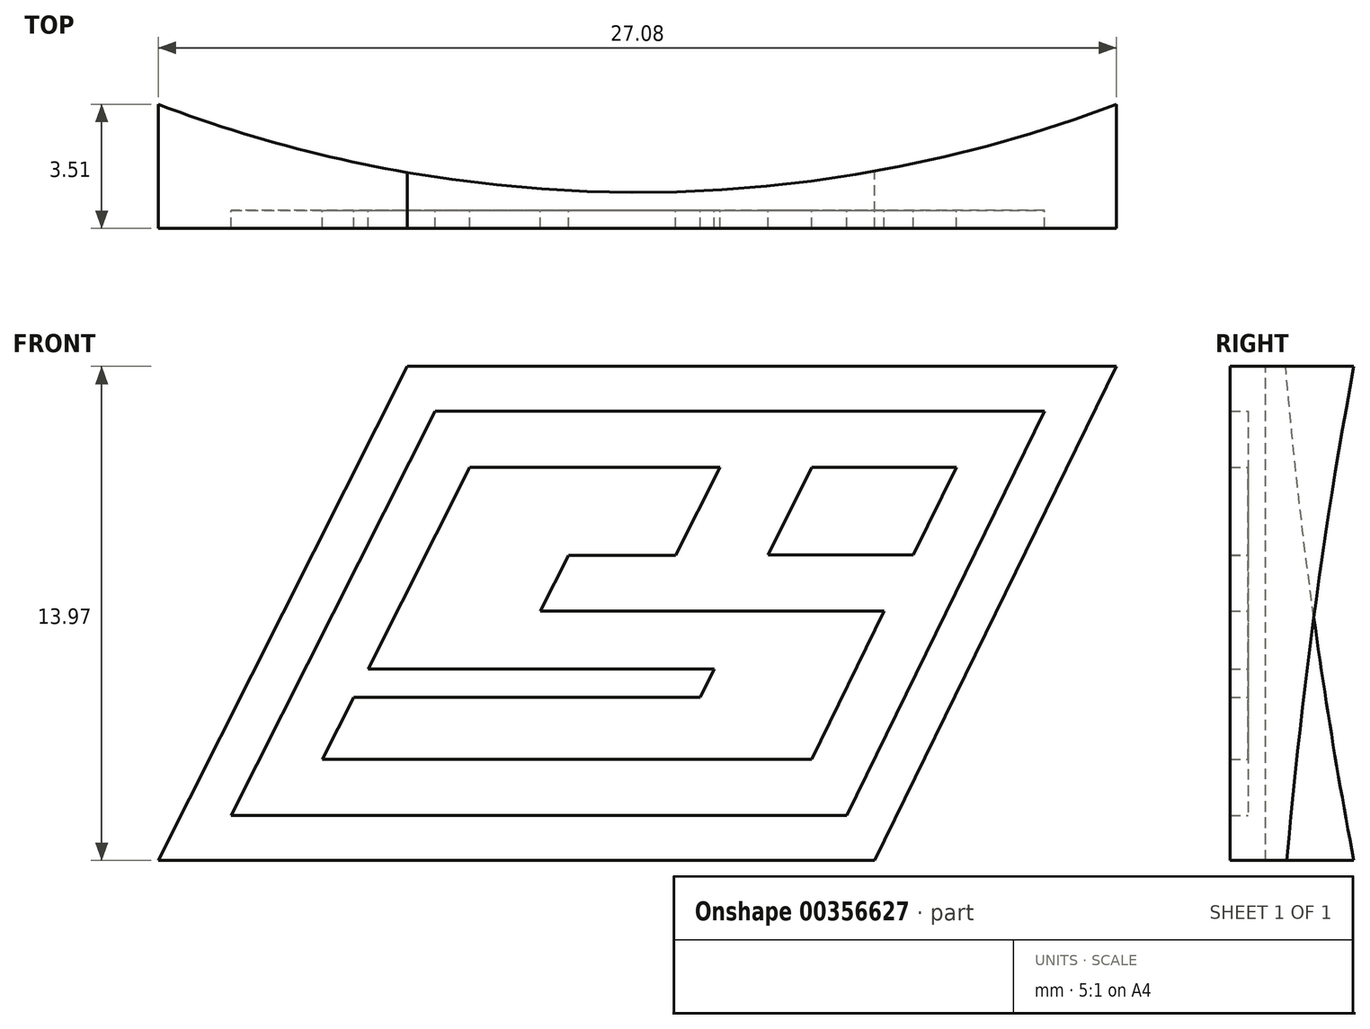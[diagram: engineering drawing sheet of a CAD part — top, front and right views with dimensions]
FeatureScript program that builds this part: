
annotation { "Feature Type Name" : "Feature", "Feature Type Description" : "" }
export const myFeature = defineFeature(function(context is Context, id is Id, definition is map)
    precondition{}
    {
        {
            var Q0;
            Q0=qCreatedBy(makeId("Front.planeOp"),FACE);
            var sketch = newSketch(context, id + "F0", { "sketchPlane" : qUnion([Q0])});
            skLineSegment(sketch, "E0", {"start": v(-12.43, 33) * mm, "end": v(15.1, 33) * mm, "construction": true});
            skLineSegment(sketch, "E1", {"start": v(15.1, 33) * mm, "end": v(6.9, 16.48) * mm, "construction": true});
            skLineSegment(sketch, "E2", {"start": v(6.9, 16.48) * mm, "end": v(-20.75, 16.48) * mm, "construction": true});
            skLineSegment(sketch, "E3", {"start": v(-20.75, 16.48) * mm, "end": v(-12.43, 33) * mm, "construction": true});
            skLineSegment(sketch, "E4", {"start": v(-12.43, 33) * mm, "end": v(1.74, 33) * mm});
            skLineSegment(sketch, "E5", {"start": v(1.74, 33) * mm, "end": v(-0.77, 28.01) * mm});
            skLineSegment(sketch, "E6", {"start": v(-0.77, 28.01) * mm, "end": v(-6.84, 28.01) * mm});
            skLineSegment(sketch, "E7", {"start": v(-6.84, 28.01) * mm, "end": v(-8.43, 24.86) * mm});
            skLineSegment(sketch, "E8", {"start": v(-8.43, 24.86) * mm, "end": v(11, 24.86) * mm});
            skPoint(sketch, "E8.endSnap0", {"position": v(11, 24.74) * mm});
            skLineSegment(sketch, "E9", {"start": v(11, 24.86) * mm, "end": v(6.9, 16.48) * mm});
            skLineSegment(sketch, "E10", {"start": v(-20.75, 16.48) * mm, "end": v(-18.97, 20) * mm});
            skLineSegment(sketch, "E11", {"start": v(-18.97, 20) * mm, "end": v(0.6, 20) * mm});
            skLineSegment(sketch, "E12", {"start": v(0.6, 20) * mm, "end": v(1.4, 21.6) * mm});
            skLineSegment(sketch, "E13", {"start": v(1.4, 21.6) * mm, "end": v(-18.16, 21.6) * mm});
            skLineSegment(sketch, "E14", {"start": v(-18.16, 21.6) * mm, "end": v(-12.43, 33) * mm});
            skLineSegment(sketch, "E15", {"start": v(6.9, 33) * mm, "end": v(4.45, 28.06) * mm});
            skLineSegment(sketch, "E16", {"start": v(4.45, 28.06) * mm, "end": v(12.65, 28.06) * mm});
            skLineSegment(sketch, "E17", {"start": v(12.65, 28.06) * mm, "end": v(15.1, 33) * mm});
            skLineSegment(sketch, "E18", {"start": v(-20.75, 16.48) * mm, "end": v(6.9, 16.48) * mm});
            skLineSegment(sketch, "E19", {"start": v(6.9, 33) * mm, "end": v(15.1, 33) * mm});
            skSolve(sketch);
        }
        {
            var Q0;
            Q0=qCreatedBy(makeId("Front.planeOp"),FACE);
            var sketch = newSketch(context, id + "F1", { "sketchPlane" : qUnion([Q0])});
            skLineSegment(sketch, "E20", {"start": v(-25.9, 13.3) * mm, "end": v(8.88, 13.3) * mm});
            skLineSegment(sketch, "E21", {"start": v(8.88, 13.3) * mm, "end": v(20.07, 36.17) * mm});
            skLineSegment(sketch, "E22", {"start": v(20.07, 36.17) * mm, "end": v(-14.38, 36.17) * mm});
            skLineSegment(sketch, "E23", {"start": v(-14.38, 36.17) * mm, "end": v(-25.9, 13.3) * mm});
            skSolve(sketch);
        }
        {
            var Q0;
            Q0=qCreatedBy(makeId("Front.planeOp"),FACE);
            var sketch = newSketch(context, id + "F2", { "sketchPlane" : qUnion([Q0])});
            skLineSegment(sketch, "E24", {"start": v(-30.02, 10.77) * mm, "end": v(-15.95, 38.71) * mm});
            skLineSegment(sketch, "E25", {"start": v(-15.95, 38.71) * mm, "end": v(24.14, 38.71) * mm});
            skLineSegment(sketch, "E26", {"start": v(24.14, 38.71) * mm, "end": v(10.47, 10.77) * mm});
            skLineSegment(sketch, "E27", {"start": v(10.47, 10.77) * mm, "end": v(-30.02, 10.77) * mm});
            skLineSegment(sketch, "E28.0", {"start": v(8.88, 13.3) * mm, "end": v(20.07, 36.17) * mm});
            skLineSegment(sketch, "E29.0", {"start": v(20.07, 36.17) * mm, "end": v(-14.38, 36.17) * mm});
            skLineSegment(sketch, "E30.0", {"start": v(-14.38, 36.17) * mm, "end": v(-25.9, 13.3) * mm});
            skLineSegment(sketch, "E31.0", {"start": v(-25.9, 13.3) * mm, "end": v(8.88, 13.3) * mm});
            skSolve(sketch);
        }
        {
            var Q0;
            Q0=makeQuery(id+"F0.imprint","IMPRINT",FACE,{"disambiguationData":[TD([[makeQuery(id+"F0.imprint","IMPRINT",EDGE,{"derivedFrom":sQuery(id+"F0.wireOp",EDGE,"E4")}),-1.0]])]});
            var Q1;
            Q1=makeQuery(id+"F0.imprint","IMPRINT",FACE,{"disambiguationData":[TD([[makeQuery(id+"F0.imprint","IMPRINT",EDGE,{"derivedFrom":sQuery(id+"F0.wireOp",EDGE,"E15")}),1.0]])]});
            extrude(context, id + "F3", {"entities" : qUnion([Q0, Q1]), "offsetDistance" : 25.4 * mm, "depth" : 2.03 * mm});
        }
        {
            var Q0;
            Q0=makeQuery(id+"F1.imprint","IMPRINT",FACE,{"disambiguationData":[TD([[makeQuery(id+"F1.imprint","IMPRINT",EDGE,{"derivedFrom":sQuery(id+"F1.wireOp",EDGE,"E20")}),1.0]])]});
            extrude(context, id + "F4", {"entities" : qUnion([Q0]), "offsetDistance" : 25.4 * mm, "depth" : 1.02 * mm});
        }
        {
            var Q0;
            Q0=makeQuery(id+"F2.imprint","IMPRINT",FACE,{"disambiguationData":[TD([[makeQuery(id+"F2.imprint","IMPRINT",EDGE,{"derivedFrom":sQuery(id+"F2.wireOp",EDGE,"E24")}),-1.0]])]});
            extrude(context, id + "F5", {"entities" : qUnion([Q0]), "operationType" : NewBodyOperationType.ADD, "offsetDistance" : 25.4 * mm, "depth" : 2.03 * mm});
        }
        {
            var Q0;
            Q0=makeQuery(id+"F4.opExtrude","SWEPT_BODY",BODY,{"disambiguationData":[OSD([sQuery(id+"F1.wireOp",EDGE,"E20"),sQuery(id+"F1.wireOp",EDGE,"E21"),sQuery(id+"F1.wireOp",EDGE,"E22"),sQuery(id+"F1.wireOp",EDGE,"E23")])]});
            var Q1;
            Q1=makeQuery(id+"F3.opExtrude","SWEPT_BODY",BODY,{"disambiguationData":[OSD([sQuery(id+"F0.wireOp",EDGE,"E4"),sQuery(id+"F0.wireOp",EDGE,"E5"),sQuery(id+"F0.wireOp",EDGE,"E6"),sQuery(id+"F0.wireOp",EDGE,"E7"),sQuery(id+"F0.wireOp",EDGE,"E8"),sQuery(id+"F0.wireOp",EDGE,"E9"),sQuery(id+"F0.wireOp",EDGE,"E10"),sQuery(id+"F0.wireOp",EDGE,"E11"),sQuery(id+"F0.wireOp",EDGE,"E12"),sQuery(id+"F0.wireOp",EDGE,"E13"),sQuery(id+"F0.wireOp",EDGE,"E14"),sQuery(id+"F0.wireOp",EDGE,"E18")])]});
            var Q2;
            Q2=makeQuery(id+"F3.opExtrude","SWEPT_BODY",BODY,{"disambiguationData":[OSD([sQuery(id+"F0.wireOp",EDGE,"E15"),sQuery(id+"F0.wireOp",EDGE,"E16"),sQuery(id+"F0.wireOp",EDGE,"E17"),sQuery(id+"F0.wireOp",EDGE,"E19")])]});
            var Q3;
            Q3=sQuery(id+"F0.wireOp",VERTEX,"E7.start");
            transform(context, id + "F6", {"entities" : qUnion([Q0, Q1, Q2]), "transformType" : TransformType.SCALE_UNIFORMLY, "scale" : .5, "scalePoint" : qUnion([Q3]), "makeCopy" : false});
        }
        {
            var Q0;
            Q0=makeQuery(id+"F5.boolean.opBoolean","MERGE",FACE,{"derivedFrom":[makeQuery(id+"F4.opExtrude","CAP_FACE",FACE,{"disambiguationData":[OSD([sQuery(id+"F1.wireOp",EDGE,"E20"),sQuery(id+"F1.wireOp",EDGE,"E21"),sQuery(id+"F1.wireOp",EDGE,"E22"),sQuery(id+"F1.wireOp",EDGE,"E23")])],"isStart":true}),makeQuery(id+"F5.opExtrude","CAP_FACE",FACE,{"disambiguationData":[OSD([sQuery(id+"F2.wireOp",EDGE,"E24"),sQuery(id+"F2.wireOp",EDGE,"E25"),sQuery(id+"F2.wireOp",EDGE,"E26"),sQuery(id+"F2.wireOp",EDGE,"E27"),sQuery(id+"F2.wireOp",EDGE,"E28.0"),sQuery(id+"F2.wireOp",EDGE,"E29.0"),sQuery(id+"F2.wireOp",EDGE,"E30.0"),sQuery(id+"F2.wireOp",EDGE,"E31.0")])],"isStart":true})]});
            extrude(context, id + "F7", {"entities" : qUnion([Q0]), "operationType" : NewBodyOperationType.ADD, "depth" : 12.7 * mm, "offsetDistance" : 25.4 * mm});
        }
        {
            var Q0;
            Q0=qCreatedBy(makeId("Front.planeOp"),FACE);
            var sketch = newSketch(context, id + "F8", { "sketchPlane" : qUnion([Q0])});
            skPoint(sketch, "E32.0", {"position": v(-18.43, 19.4) * mm});
            skPoint(sketch, "E33.0", {"position": v(8.65, 33.36) * mm});
            skLineSegment(sketch, "E34", {"start": v(-18.43, 19.4) * mm, "end": v(-18.43, 33.36) * mm, "construction": true});
            skLineSegment(sketch, "E35", {"start": v(-18.43, 33.36) * mm, "end": v(8.65, 33.36) * mm, "construction": true});
            skLineSegment(sketch, "E36", {"start": v(8.65, 19.4) * mm, "end": v(8.65, 33.36) * mm, "construction": true});
            skLineSegment(sketch, "E37", {"start": v(8.65, 19.4) * mm, "end": v(-18.43, 19.4) * mm, "construction": true});
            skPoint(sketch, "E38", {"position": v(-4.89, 33.36) * mm});
            skSolve(sketch);
        }
        {
            var Q0;
            {var subQ0=sQuery(id+"F2.wireOp",EDGE,"E25");Q0=makeQuery(id+"F7.boolean.opBoolean","MERGE",FACE,{"derivedFrom":[makeQuery(id+"F5.opExtrude","SWEPT_FACE",FACE,{"disambiguationData":[OSD([subQ0])]}),makeQuery(id+"F7.opExtrude","SWEPT_FACE",FACE,{"disambiguationData":[OSD([subQ0])]})]});}
            var sketch = newSketch(context, id + "F9", { "sketchPlane" : qUnion([Q0])});
            skPoint(sketch, "E39.0", {"position": v(-4.89, 0) * mm});
            skPoint(sketch, "E40.0", {"position": v(-18.43, -1.02) * mm});
            skLineSegment(sketch, "E41.0", {"start": v(8.65, 0) * mm, "end": v(-18.43, 0) * mm});
            skPoint(sketch, "E42.0", {"position": v(8.65, -1.02) * mm});
            skCircle(sketch, "E43", {"center": v(-4.89, 38.1) * mm, "radius": 38.1 * mm});
            skSolve(sketch);
        }
        {
            var Q0;
            Q0 = qSketchRegion(id + "F9", true);
            extrude(context, id + "F10", {"entities" : qUnion([Q0]), "operationType" : NewBodyOperationType.REMOVE, "oppositeDirection" : true, "depth" : 25.4 * mm, "offsetDistance" : 25.4 * mm});
        }
    });
